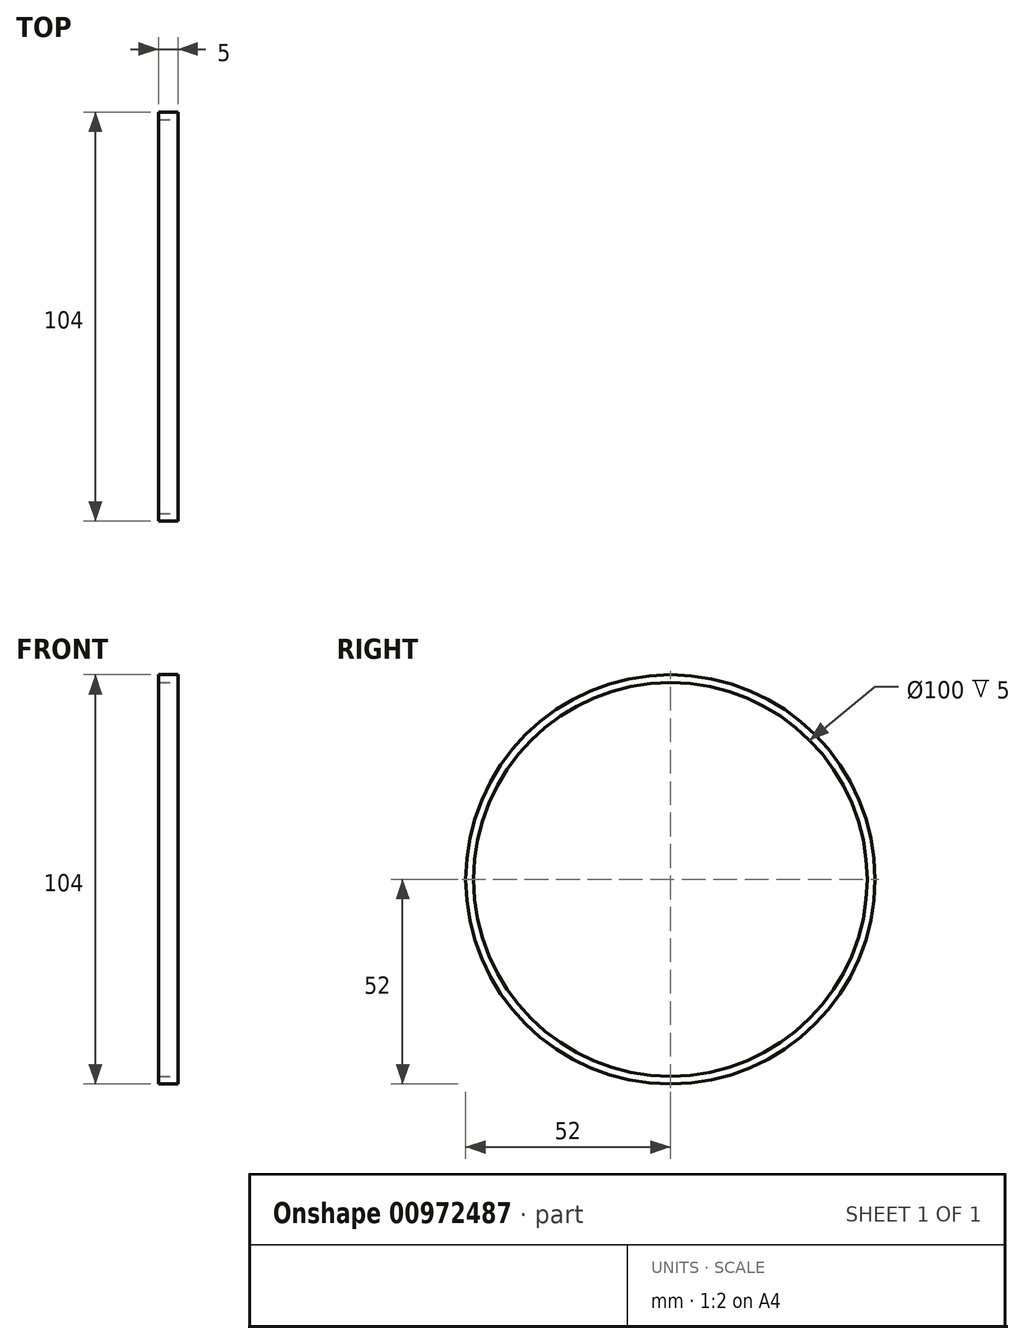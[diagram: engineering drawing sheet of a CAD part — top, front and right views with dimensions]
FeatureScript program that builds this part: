
annotation { "Feature Type Name" : "Feature", "Feature Type Description" : "" }
export const myFeature = defineFeature(function(context is Context, id is Id, definition is map)
    precondition{}
    {
        {
            var Q0;
            Q0=qCreatedBy(makeId("Front.planeOp"),FACE);
            var sketch = newSketch(context, id + "F0", { "sketchPlane" : qUnion([Q0])});
            skLineSegment(sketch, "E0", {"start": v(0, 0) * mm, "end": v(-79.76, 0) * mm, "construction": true});
            skLineSegment(sketch, "E1", {"start": v(0, 52) * mm, "end": v(-5, 52) * mm});
            skLineSegment(sketch, "E2", {"start": v(-5, 52) * mm, "end": v(-5, 50) * mm});
            skLineSegment(sketch, "E3", {"start": v(-5, 50) * mm, "end": v(0, 50) * mm});
            skLineSegment(sketch, "E4", {"start": v(0, 50) * mm, "end": v(0, 52) * mm});
            skSolve(sketch);
        }
        {
            var Q0;
            Q0=qSketchRegion(id+"F0",true);
            var Q1;
            Q1=sQuery(id+"F0.wireOp",EDGE,"E0");
            revolve(context, id + "F1", {"surfaceOperationType" : NewSurfaceOperationType.NEW, "entities" : qUnion([Q0]), "axis" : qUnion([Q1]), "revolveType" : RevolveType.FULL});
        }
    });
